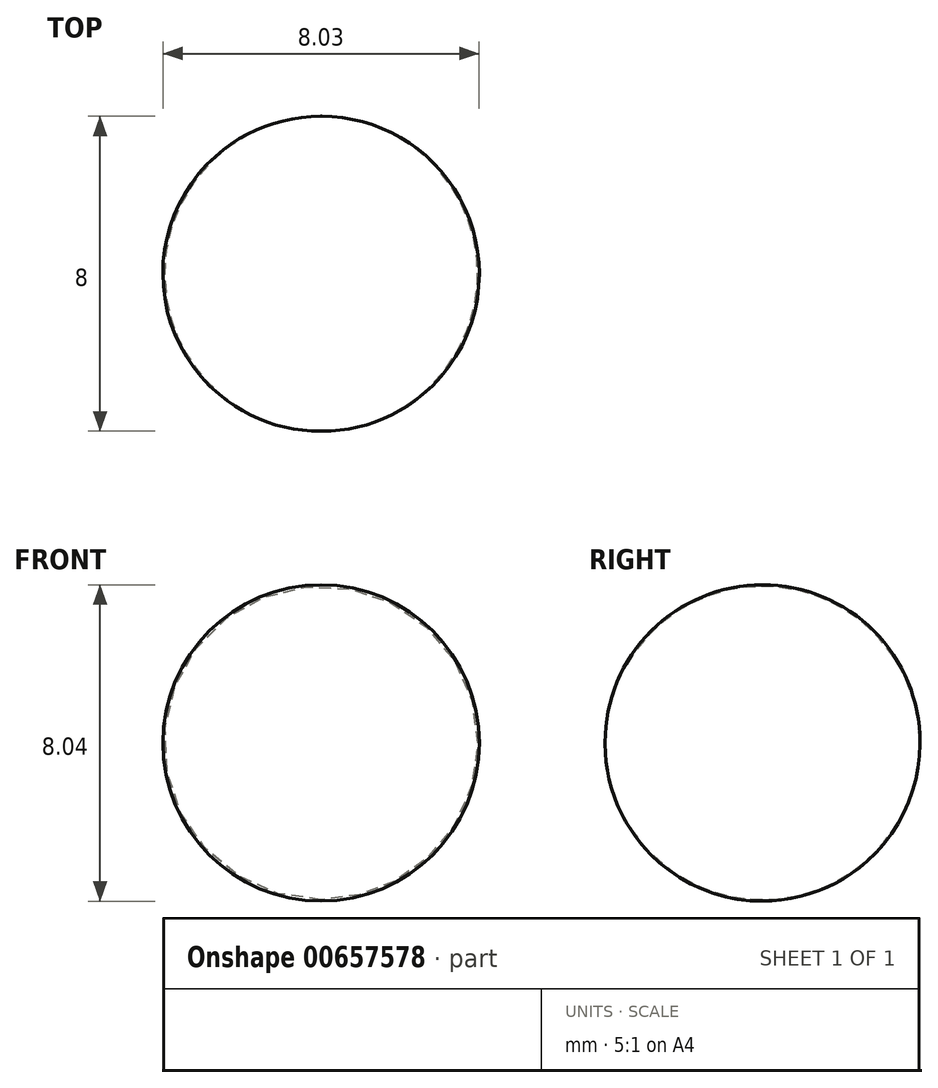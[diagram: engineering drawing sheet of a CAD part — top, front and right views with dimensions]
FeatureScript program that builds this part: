
annotation { "Feature Type Name" : "Feature", "Feature Type Description" : "" }
export const myFeature = defineFeature(function(context is Context, id is Id, definition is map)
    precondition{}
    {
        {
            var Q0;
            Q0=qCreatedBy(makeId("Top.planeOp"),FACE);
            var sketch = newSketch(context, id + "F0", { "sketchPlane" : qUnion([Q0])});
            skLineSegment(sketch, "E0", {"start": v(-14.5, 8) * mm, "end": v(-14.5, 0) * mm});
            skArc(sketch, "E1", {"start": v(-14.5, 0) * mm, "mid": v(-10.51, 4) * mm, "end": v(-14.5, 8) * mm});
            skSolve(sketch);
        }
        {
            var Q0;
            Q0=makeQuery(id+"F0.imprint","IMPRINT",FACE,{"disambiguationData":[TD([[makeQuery(id+"F0.imprint","IMPRINT",EDGE,{"derivedFrom":sQuery(id+"F0.wireOp",EDGE,"E0")}),1.0]])]});
            var Q1;
            Q1=sQuery(id+"F0.wireOp",EDGE,"E0");
            revolve(context, id + "F1", {"entities" : qUnion([Q0]), "axis" : qUnion([Q1]), "revolveType" : RevolveType.FULL});
        }
    });
